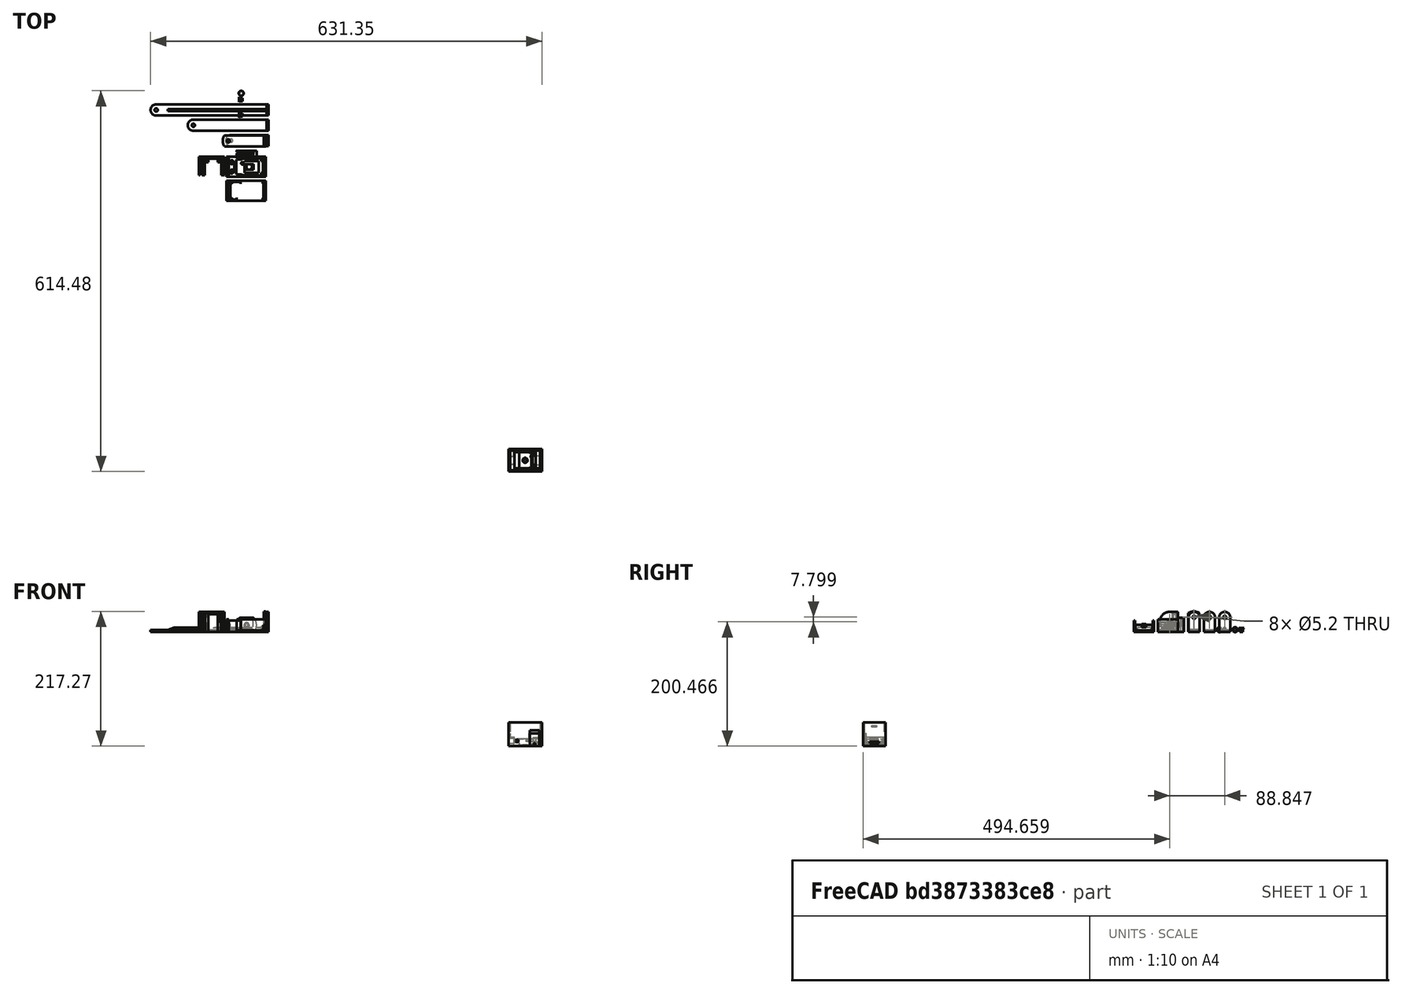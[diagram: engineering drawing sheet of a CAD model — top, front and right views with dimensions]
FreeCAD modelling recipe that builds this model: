
FCSTD DOCUMENT  (FreeCAD 0.18.4R)
Label: camera.wroover.nested
License: All rights reserved
LicenseURL: http://en.wikipedia.org/wiki/All_rights_reserved
objects: Part::Feature×27, Part::Extrusion×26, Part::FeaturePython×26, Part::Part2DObjectPython×23, Part::MultiFuse×20, Part::Cut×15, App::DocumentObjectGroup×10, Part::Cone×2
note: 139 computed .brp shape members not serialized (recipe doc carries the construction recipe); baked Part::Feature solids carry a one-line shape summary decoded from their .brp

FEATURE [Part::MultiFuse] Fusion005002002014004003003002009002010004002003006003008008004007002004008002005003003004011  label="Rail-Straight"
FEATURE [Part::Feature] Face
  Placement = pos=(-49.1911,484.37,17.9321) rot=(1,0,0;3.14159rad)
  shape: bbox 2.889e-06 x 7.275 x 8.4 mm, 1 faces, 0 solids (baked)
FEATURE [Part::Extrusion] Extrusion
  Base = -> Face
  Dir = (0.2,-6e-16,8e-16)
  DirMode = 0
  FaceMakerClass = Part::FaceMakerBullseye
  LengthFwd = 0
  LengthRev = 0
  Solid = true
  Symmetric = false
FEATURE [Part::MultiFuse] Fusion
  Shapes = -> [Extrusion,Fusion005002002014004003003002009002010004002003006003008008004007002004008002005003003004011]
FEATURE [Part::Feature] Face001
  Placement = pos=(-641.855,484.37,-5.97e-13) rot=(0,0,1;3.14159rad)
  shape: bbox 2.889e-06 x 7.275 x 8.4 mm, 1 faces, 0 solids (baked)
FEATURE [Part::Extrusion] Extrusion001
  Base = -> Face001
  Dir = (-0.2,-6e-16,-8e-16)
  DirMode = 0
  FaceMakerClass = Part::FaceMakerBullseye
  LengthFwd = 0
  LengthRev = 0
  Solid = true
  Symmetric = false
FEATURE [Part::MultiFuse] Fusion005002002014004003003002009002010004002003006003008008004007002004008002005003003004012
  Shapes = -> [Fusion,Extrusion001]
FEATURE [Part::Part2DObjectPython] Rectangle  # Draft 2D object (typed FeaturePython)
  ChamferSize = 0
  Columns = 1
  FilletRadius = 0
  Height = 80
  Length = 77
  MakeFace = true
  Placement = pos=(-363.417,362.38,-31.0339) rot=(0.57735,-0.57735,-0.57735;2.0944rad)
  Rows = 1
  Support = -> [Fusion005002002014004003003002009002010004002003006003008008004007002004008002005003003004012]
FEATURE [Part::FeaturePython] Slice  # WARN: FeaturePython — macro-defined, semantics opaque (R4)
  Base = -> Fusion005002002014004003003002009002010004002003006003008008004007002004008002005003003004012
  Mode = 1
  Tolerance = 0
  Tools = -> [Rectangle]
FEATURE [Part::FeaturePython] Slice_child0  label="Slice.0"  # WARN: FeaturePython — macro-defined, semantics opaque (R4)
  Base = -> Slice
  FilterType = 1
  Invert = false
  OverrideMaxVal = 0
  WindowFrom = 80
  WindowTo = 100
  items = 0
FEATURE [Part::FeaturePython] Slice_child1  label="Slice.1"  # WARN: FeaturePython — macro-defined, semantics opaque (R4)
  Base = -> Slice
  FilterType = 1
  Invert = false
  OverrideMaxVal = 0
  Placement = pos=(-3,0,-4e-15) rot=(0,0,1;0rad)
  WindowFrom = 80
  WindowTo = 100
  items = 1
FEATURE [Part::MultiFuse] Fusion005002002014004003003002009002010004002003006003008008004007002004008002005003003004009  label="Console"
  Placement = pos=(66.1287,37.5114,-1.47e-13) rot=(0,0,1;0rad)
FEATURE [Part::Part2DObjectPython] Rectangle001  # Draft 2D object (typed FeaturePython)
  ChamferSize = 0
  Columns = 1
  FilletRadius = 0
  Height = 49.0124
  Length = 71.1879
  MakeFace = true
  Placement = pos=(-260.782,380.747,-18.9904) rot=(0.57735,0.57735,0.57735;2.0944rad)
  Rows = 1
  Support = -> [Fusion005002002014004003003002009002010004002003006003008008004007002004008002005003003004009]
FEATURE [Part::Part2DObjectPython] Rectangle002  # Draft 2D object (typed FeaturePython)
  ChamferSize = 0
  Columns = 1
  FilletRadius = 0
  Height = 109.957
  Length = 144.352
  MakeFace = true
  Placement = pos=(-370.958,471.32,-6.63395) rot=(1,0,0;3.14159rad)
  Rows = 1
  Support = -> [Fusion005002002014004003003002009002010004002003006003008008004007002004008002005003003004009]
FEATURE [Part::FeaturePython] Slice001  # WARN: FeaturePython — macro-defined, semantics opaque (R4)
  Base = -> Fusion005002002014004003003002009002010004002003006003008008004007002004008002005003003004009
  Mode = 1
  Tolerance = 0
  Tools = -> [Rectangle002]
FEATURE [Part::FeaturePython] Slice001_child0  label="Slice001.0"  # WARN: FeaturePython — macro-defined, semantics opaque (R4)
  Base = -> Slice001
  FilterType = 1
  Invert = false
  OverrideMaxVal = 0
  WindowFrom = 80
  WindowTo = 100
  items = 0
FEATURE [App::DocumentObjectGroup] GrExplode_Slice001  label="Exploded Slice001"
  Group = -> [Slice001_child0]
FEATURE [Part::FeaturePython] Slice002  # WARN: FeaturePython — macro-defined, semantics opaque (R4)
  Base = -> Slice001_child0
  Mode = 1
  Tolerance = 0
  Tools = -> [Rectangle001]
FEATURE [Part::FeaturePython] Slice002_child0  label="Slice002.0"  # WARN: FeaturePython — macro-defined, semantics opaque (R4)
  Base = -> Slice002
  FilterType = 1
  Invert = false
  OverrideMaxVal = 0
  Placement = pos=(0,-35.1536,2.389e-13) rot=(0,0,1;0rad)
  WindowFrom = 80
  WindowTo = 100
  items = 0
FEATURE [App::DocumentObjectGroup] GrExplode_Slice002  label="Exploded Slice002"
  Group = -> [Slice002_child0]
FEATURE [Part::Part2DObjectPython] Rectangle003  # Draft 2D object (typed FeaturePython)
  ChamferSize = 0
  Columns = 1
  FilletRadius = 0
  Height = 32.2
  Length = 3.39945
  MakeFace = true
  Placement = pos=(-363.417,339.38,-7.13395) rot=(0.57735,-0.57735,-0.57735;2.0944rad)
  Rows = 1
  Support = -> [Slice_child0]
FEATURE [Part::Extrusion] Extrusion002
  Base = -> Rectangle003
  Dir = (-3,0,0)
  DirMode = 0
  FaceMakerClass = Part::FaceMakerBullseye
  LengthFwd = 0
  LengthRev = 0
  Solid = true
  Symmetric = false
FEATURE [Part::Part2DObjectPython] Wire  # Draft 2D object (typed FeaturePython)
  ChamferSize = 0
  Closed = true
  End = (-332.03,322.443,11.0661)
  FilletRadius = 0
  Length = 25.2
  MakeFace = true
  Placement = pos=(-332.03,322.443,6.86605) rot=(0.57735,-0.57735,-0.57735;2.0944rad)
  Points = (6) [(0,0,0),(-3.63731,-2.1,5.68434e-14),(-7.27461,3.4639e-14,5.68434e-14),(-7.27461,4.2,1.13687e-13),(-3.63731,6.3,1.13687e-13),(5.68434e-14,4.2,5.68434e-14)]
  Start = (-332.03,322.443,6.86605)
  Subdivisions = 0
  Support = -> [Slice_child0]
FEATURE [Part::Extrusion] Extrusion003
  Base = -> Wire
  Dir = (4.9,3.83e-14,4.42e-14)
  DirMode = 0
  FaceMakerClass = Part::FaceMakerBullseye
  LengthFwd = 0
  LengthRev = 0
  Solid = true
  Symmetric = false
FEATURE [Part::MultiFuse] Fusion005002002014004003003002009002010004002003006003008008004007002004008002005003003004013
  Shapes = -> [Slice_child0,Extrusion003]
FEATURE [Part::Feature] Fusion005002002014004003003002009002010004002003006003008008004007002004008002005003003004013001  label="Fusion005002002014004003003002009002010004002003006003008008004007002004008002005003003004014"
  shape: bbox 36.29 x 29.4 x 32.2 mm, 46 faces (baked)
FEATURE [Part::Feature] Face002
  shape: bbox 3.089e-06 x 29.4 x 32.2 mm, 1 faces, 0 solids (baked)
FEATURE [Part::Extrusion] Extrusion004
  Base = -> Face002
  Dir = (-1.9,-6.1e-15,-2.5e-15)
  DirMode = 0
  FaceMakerClass = Part::FaceMakerBullseye
  LengthFwd = 0
  LengthRev = 0
  Solid = true
  Symmetric = false
FEATURE [Part::Cut] Cut
  Base = -> Fusion005002002014004003003002009002010004002003006003008008004007002004008002005003003004013001
  Tool = -> Extrusion004
FEATURE [Part::Feature] Face003
  Placement = pos=(-48.7911,184.728,1.61e-13) rot=(0,0,1;0rad)
  shape: bbox 2.989e-06 x 29.4 x 32.2 mm, 1 faces, 0 solids (baked)
FEATURE [Part::Extrusion] Extrusion005
  Base = -> Face003
  Dir = (-1.5,4.8e-15,-2e-15)
  DirMode = 0
  FaceMakerClass = Part::FaceMakerBullseye
  LengthFwd = 0
  LengthRev = 0
  Solid = true
  Symmetric = false
FEATURE [Part::MultiFuse] Fusion005002002014004003003002009002010004002003006003008008004007002004008002005003003004013002
  Shapes = -> [Extrusion005,Slice_child1]
FEATURE [Part::MultiFuse] Fusion005002002014004003003002009002010004002003006003008008004007002004008002005003003004013003
  Shapes = -> [Fusion005002002014004003003002009002010004002003006003008008004007002004008002005003003004013002,Extrusion002,Cut]
FEATURE [App::DocumentObjectGroup] GrExplode_Slice  label="Exploded Slice"
  Group = -> [Fusion005002002014004003003002009002010004002003006003008008004007002004008002005003003004013,Fusion005002002014004003003002009002010004002003006003008008004007002004008002005003003004013003]
FEATURE [Part::Feature] Fusion005002002014004003003002009002010004002003006003008008004007002004008002005003003004013003001  label="Fusion005002002014004003003002009002010004002003006003008008004007002004008002005003003004013004"
  shape: bbox 39.39 x 29.4 x 32.2 mm, 51 faces (baked)
FEATURE [Part::Cone] Cone
  Angle = 360
  AttacherType = Attacher::AttachEngine3D
  Height = 2
  Placement = pos=(-301.953,406.671,-3.63395) rot=(0,-1,0;1.5708rad)
  Radius1 = 2.6
  Radius2 = 4
FEATURE [Part::Cone] Cone001
  Angle = 360
  AttacherType = Attacher::AttachEngine3D
  Height = 2
  Placement = pos=(-366.417,326.16,8.96605) rot=(0,-1,0;1.5708rad)
  Radius1 = 2.6
  Radius2 = 4
FEATURE [Part::Cut] Cut001
  Base = -> Fusion005002002014004003003002009002010004002003006003008008004007002004008002005003003004013003001
  Tool = -> Cone001
FEATURE [Part::Part2DObjectPython] Rectangle004  # Draft 2D object (typed FeaturePython)
  ChamferSize = 0
  Columns = 1
  FilletRadius = 0
  Height = 140.382
  Length = 142.339
  MakeFace = true
  Placement = pos=(-376.002,355.088,66.5569) rot=(-1,0,0;1.5708rad)
  Rows = 1
FEATURE [Part::Part2DObjectPython] Rectangle005  # Draft 2D object (typed FeaturePython)
  ChamferSize = 0
  Columns = 1
  FilletRadius = 0
  Height = 140.382
  Length = 142.339
  MakeFace = true
  Placement = pos=(-376.002,375.088,66.5569) rot=(-1,0,0;1.5708rad)
  Rows = 1
FEATURE [Part::FeaturePython] Slice003  # WARN: FeaturePython — macro-defined, semantics opaque (R4)
  Base = -> Slice002_child0
  Mode = 1
  Tolerance = 0
  Tools = -> [Rectangle005]
FEATURE [Part::FeaturePython] Slice003_child0  label="Slice003.0"  # WARN: FeaturePython — macro-defined, semantics opaque (R4)
  Base = -> Slice003
  FilterType = 1
  Invert = false
  OverrideMaxVal = 0
  WindowFrom = 80
  WindowTo = 100
  items = 0
FEATURE [App::DocumentObjectGroup] GrExplode_Slice003  label="Exploded Slice003"
  Group = -> [Slice003_child0]
FEATURE [Part::FeaturePython] Slice004  # WARN: FeaturePython — macro-defined, semantics opaque (R4)
  Base = -> Slice003_child0
  Mode = 1
  Tolerance = 0
  Tools = -> [Rectangle004]
FEATURE [Part::FeaturePython] Slice004_child0  label="Slice004.0"  # WARN: FeaturePython — macro-defined, semantics opaque (R4)
  Base = -> Slice004
  FilterType = 1
  Invert = false
  OverrideMaxVal = 0
  WindowFrom = 80
  WindowTo = 100
  items = 0
FEATURE [Part::Part2DObjectPython] Circle001  # Draft 2D object (typed FeaturePython)
  FirstAngle = 0
  LastAngle = 0
  MakeFace = true
  Placement = pos=(-263.782,365.088,9.58564) rot=(0.57735,-0.57735,-0.57735;2.0944rad)
  Radius = 4
FEATURE [Part::Extrusion] Extrusion006
  Base = -> Circle001
  Dir = (3,0,0)
  DirMode = 0
  FaceMakerClass = Part::FaceMakerBullseye
  LengthFwd = 0
  LengthRev = 0
  Solid = true
  Symmetric = false
FEATURE [Part::MultiFuse] Fusion005002002014004003003002009002010004002003006003008008004007002004008002005003003004013003002
  Shapes = -> [Slice004_child0,Extrusion006]
FEATURE [Part::Part2DObjectPython] Circle002  # Draft 2D object (typed FeaturePython)
  FirstAngle = 0
  LastAngle = 0
  MakeFace = true
  Placement = pos=(-301.953,406.671,-3.63395) rot=(0.57735,0.57735,0.57735;2.0944rad)
  Radius = 2.6
  Support = -> [Cone]
FEATURE [Part::Extrusion] Extrusion007
  Base = -> Circle002
  Dir = (4,0,0)
  DirMode = 0
  FaceMakerClass = Part::FaceMakerBullseye
  LengthFwd = 0
  LengthRev = 0
  Solid = true
  Symmetric = false
FEATURE [Part::MultiFuse] Fusion005002002014004003003002009002010004002003006003008008004007002004008002005003003004013003003
  Placement = pos=(0,25.1211,0) rot=(0,0,1;0rad)
  Shapes = -> [Cone,Extrusion007]
FEATURE [Part::MultiFuse] Fusion005002002014004003003002009002010004002003006003008008004007002004008002005003003004013003004
  Shapes = -> [Cone,Extrusion007]
FEATURE [Part::MultiFuse] Fusion005002002014004003003002009002010004002003006003008008004007002004008002005003003004013003005
  Placement = pos=(-64.6671,-80.5121,12.6) rot=(0,0,1;0rad)
  Shapes = -> [Cone,Extrusion007]
FEATURE [Part::Feature] Fusion005002002014004003003002009002010004002003006003008008004007002004008002005003003004013003004001  label="Fusion005002002014004003003002009002010004002003006003008008004007002004008002005003003004013003006"
  Placement = pos=(40.1704,-41.5836,20.3995) rot=(0,0,1;0rad)
  shape: bbox 6 x 8 x 8 mm, 4 faces (baked)
FEATURE [Part::Cut] Cut002
  Base = -> Fusion005002002014004003003002009002010004002003006003008008004007002004008002005003003004013003002
  Tool = -> Fusion005002002014004003003002009002010004002003006003008008004007002004008002005003003004013003004001
FEATURE [App::DocumentObjectGroup] GrExplode_Slice004  label="Exploded Slice004"
  Group = -> [Cut002]
FEATURE [Part::Part2DObjectPython] Rectangle006  # Draft 2D object (typed FeaturePython)
  ChamferSize = 0
  Columns = 1
  FilletRadius = 0
  Height = 141.963
  Length = 167.182
  MakeFace = true
  Placement = pos=(-347.373,356.088,87.747) rot=(-1,0,0;1.5708rad)
  Rows = 1
  Support = -> [Cut002]
FEATURE [Part::Part2DObjectPython] Rectangle007  # Draft 2D object (typed FeaturePython)
  ChamferSize = 0
  Columns = 1
  FilletRadius = 0
  Height = 141.963
  Length = 167.182
  MakeFace = true
  Placement = pos=(-347.373,374.088,87.747) rot=(-1,0,0;1.5708rad)
  Rows = 1
  Support = -> [Cut002]
FEATURE [Part::FeaturePython] Slice005  # WARN: FeaturePython — macro-defined, semantics opaque (R4)
  Base = -> Cut002
  Mode = 1
  Tolerance = 0
  Tools = -> [Rectangle007]
FEATURE [Part::FeaturePython] Slice005_child0  label="Slice005.0"  # WARN: FeaturePython — macro-defined, semantics opaque (R4)
  Base = -> Slice005
  FilterType = 1
  Invert = false
  OverrideMaxVal = 0
  WindowFrom = 80
  WindowTo = 100
  items = 0
FEATURE [App::DocumentObjectGroup] GrExplode_Slice005  label="Exploded Slice005"
  Group = -> [Slice005_child0]
FEATURE [Part::FeaturePython] Slice006  # WARN: FeaturePython — macro-defined, semantics opaque (R4)
  Base = -> Slice005_child0
  Mode = 1
  Tolerance = 0
  Tools = -> [Rectangle006]
FEATURE [Part::FeaturePython] Slice006_child0  label="Slice006.0"  # WARN: FeaturePython — macro-defined, semantics opaque (R4)
  Base = -> Slice006
  FilterType = 1
  Invert = false
  OverrideMaxVal = 0
  WindowFrom = 80
  WindowTo = 100
  items = 0
FEATURE [Part::Cut] Cut003  label="Frame"
  Tool = -> Extrusion
FEATURE [Part::Part2DObjectPython] Circle003  # Draft 2D object (typed FeaturePython)
  FirstAngle = 0
  LastAngle = 0
  MakeFace = true
  Placement = pos=(-263.782,365.088,16.7655) rot=(0.57735,-0.57735,-0.57735;2.0944rad)
  Radius = 4
FEATURE [Part::Extrusion] Extrusion008
  Base = -> Circle003
  Dir = (2,0,0)
  DirMode = 0
  FaceMakerClass = Part::FaceMakerBullseye
  LengthFwd = 0
  LengthRev = 0
  Solid = true
  Symmetric = false
FEATURE [Part::MultiFuse] Fusion005002002014004003003002009002010004002003006003008008004007002004008002005003003004013003004002
  Shapes = -> [Extrusion008,Slice006_child0]
FEATURE [Part::Part2DObjectPython] Circle004  # Draft 2D object (typed FeaturePython)
  FirstAngle = 0
  LastAngle = 0
  MakeFace = true
  Placement = pos=(-260.782,365.088,16.7655) rot=(0.57735,0.57735,0.57735;2.0944rad)
  Radius = 2.6
FEATURE [Part::Extrusion] Extrusion009
  Base = -> Circle004
  Dir = (-9.48538,0,0)
  DirMode = 0
  FaceMakerClass = Part::FaceMakerBullseye
  LengthFwd = 0
  LengthRev = 0
  Solid = true
  Symmetric = false
FEATURE [Part::Cut] Cut004
  Base = -> Fusion005002002014004003003002009002010004002003006003008008004007002004008002005003003004013003004002
  Tool = -> Extrusion009
FEATURE [Part::Feature] Face004
  shape: bbox 32.2 x 4.069e-06 x 22.84 mm, 1 faces, 0 solids (baked)
FEATURE [Part::Feature] Face005
  Placement = pos=(-2.1881e-12,3,2.9e-14) rot=(0,0,1;0rad)
  shape: bbox 32.2 x 4.069e-06 x 22.84 mm, 1 faces, 0 solids (baked)
FEATURE [Part::Extrusion] Extrusion011
  Base = -> Face005
  Dir = (-1.4587e-12,2,1.94e-14)
  DirMode = 0
  FaceMakerClass = Part::FaceMakerBullseye
  LengthFwd = 0
  LengthRev = 0
  Solid = true
  Symmetric = false
FEATURE [Part::Part2DObjectPython] Rectangle008  # Draft 2D object (typed FeaturePython)
  ChamferSize = 0
  Columns = 1
  FilletRadius = 0
  Height = 132.663
  Length = 70.7455
  MakeFace = true
  Placement = pos=(-281.653,308.795,-48.4256) rot=(0.57735,0.57735,0.57735;2.0944rad)
  Rows = 1
  Support = -> [Cut003]
FEATURE [Part::FeaturePython] Slice007  # WARN: FeaturePython — macro-defined, semantics opaque (R4)
  Base = -> Extrusion011
  Mode = 1
  Tolerance = 0
  Tools = -> [Rectangle008]
FEATURE [Part::FeaturePython] Slice007_child0  label="Slice007.0"  # WARN: FeaturePython — macro-defined, semantics opaque (R4)
  Base = -> Slice007
  FilterType = 1
  Invert = false
  OverrideMaxVal = 0
  WindowFrom = 80
  WindowTo = 100
  items = 0
FEATURE [Part::FeaturePython] Slice007_child1  label="Slice007.1"  # WARN: FeaturePython — macro-defined, semantics opaque (R4)
  Base = -> Slice007
  FilterType = 1
  Invert = false
  OverrideMaxVal = 0
  WindowFrom = 80
  WindowTo = 100
  items = 1
FEATURE [Part::Feature] Face006
  shape: bbox 6.28 x 4.169e-06 x 22.84 mm, 1 faces, 0 solids (baked)
FEATURE [Part::Extrusion] Extrusion012
  Base = -> Face006
  Dir = (2.1881e-12,-3,-2.9e-14)
  DirMode = 0
  FaceMakerClass = Part::FaceMakerBullseye
  LengthFwd = 0
  LengthRev = 0
  Solid = true
  Symmetric = false
FEATURE [Part::Feature] Face007
  shape: bbox 6.28 x 4.169e-06 x 22.84 mm, 1 faces, 0 solids (baked)
FEATURE [Part::Extrusion] Extrusion013
  Base = -> Face007
  Dir = (-1.459e-13,0.2,1.9e-15)
  DirMode = 0
  FaceMakerClass = Part::FaceMakerBullseye
  LengthFwd = 0
  LengthRev = 0
  Solid = true
  Symmetric = false
FEATURE [Part::Feature] Face008
  shape: bbox 25.92 x 4.169e-06 x 22.84 mm, 1 faces, 0 solids (baked)
FEATURE [Part::Extrusion] Extrusion014
  Base = -> Face008
  Dir = (-1.459e-13,0.2,1.9e-15)
  DirMode = 0
  FaceMakerClass = Part::FaceMakerBullseye
  LengthFwd = 0
  LengthRev = 0
  Solid = true
  Symmetric = false
FEATURE [Part::MultiFuse] Fusion005002002014004003003002009002010004002003006003008008004007002004008002005003003004013003004003
  Shapes = -> [Extrusion014,Extrusion013,Slice007_child1,Slice007_child0,Extrusion012,Cut003]
FEATURE [Part::Feature] Face009
  shape: bbox 3.089e-06 x 29.4 x 32.2 mm, 1 faces, 0 solids (baked)
FEATURE [Part::Extrusion] Extrusion015
  Base = -> Face009
  Dir = (-0.202869,7e-16,-3e-16)
  DirMode = 0
  FaceMakerClass = Part::FaceMakerBullseye
  LengthFwd = 0
  LengthRev = 0
  Solid = true
  Symmetric = false
FEATURE [Part::Part2DObjectPython] Circle005  # Draft 2D object (typed FeaturePython)
  FirstAngle = 0
  LastAngle = 0
  MakeFace = true
  Placement = pos=(-368.62,326.159,8.96605) rot=(0.57735,-0.57735,-0.57735;2.0944rad)
  Radius = 4
FEATURE [Part::Extrusion] Extrusion016
  Base = -> Circle005
  Dir = (2.20287,0,0)
  DirMode = 0
  FaceMakerClass = Part::FaceMakerBullseye
  LengthFwd = 0
  LengthRev = 0
  Solid = true
  Symmetric = false
FEATURE [Part::MultiFuse] Fusion005002002014004003003002009002010004002003006003008008004007002004008002005003003004013003004004
  Shapes = -> [Extrusion015,Extrusion016]
FEATURE [Part::MultiFuse] Fusion005002002014004003003002009002010004002003006003008008004007002004008002005003003004013003004005
  Shapes = -> [Fusion005002002014004003003002009002010004002003006003008008004007002004008002005003003004013003004004,Cut001]
FEATURE [Part::Cut] Cut005
  Base = -> Fusion005002002014004003003002009002010004002003006003008008004007002004008002005003003004013003004005
  Tool = -> Fusion005002002014004003003002009002010004002003006003008008004007002004008002005003003004013003005
FEATURE [Part::Feature] Fusion005002002014004003003002009002010004002003006003008008004007002004008002005003003004013003003001  label="Fusion005002002014004003003002009002010004002003006003008008004007002004008002005003003004013003004006"
  Placement = pos=(-723.266,45.4151,7.39306) rot=(0,0,-1;1.5708rad)
  shape: bbox 8 x 6 x 8 mm, 4 faces (baked)
FEATURE [Part::Feature] Fusion005002002014004003003002009002010004002003006003008008004007002004008002005003003004013003004006  label="Fusion005002002014004003003002009002010004002003006003008008004007002004008002005003003004013003004007"
  shape: bbox 6 x 8 x 8 mm, 4 faces (baked)
FEATURE [Part::Feature] Fusion005002002014004003003002009002010004002003006003008008004007002004008002005003003004013003004007  label="Fusion005002002014004003003002009002010004002003006003008008004007002004008002005003003004013003004008"
  Placement = pos=(-296.517,10.1875,-305.087) rot=(0,1,0;1.5708rad)
  shape: bbox 8 x 8 x 6 mm, 4 faces (baked)
FEATURE [Part::Cut] Cut006
  Base = -> Fusion005002002014004003003002009002010004002003006003008008004007002004008002005003003004013003004003
  Tool = -> Fusion005002002014004003003002009002010004002003006003008008004007002004008002005003003004013003003001
FEATURE [App::DocumentObjectGroup] GrExplode_Slice007  label="Exploded Slice007"
  Group = -> [Cut006]
FEATURE [Part::Part2DObjectPython] Circle006  # Draft 2D object (typed FeaturePython)
  FirstAngle = 0
  LastAngle = 0
  MakeFace = true
  Placement = pos=(-313.782,365.088,-3.63395) rot=(0,0,1;0rad)
  Radius = 4
  Support = -> [Cut004]
FEATURE [Part::Extrusion] Extrusion017
  Base = -> Circle006
  Dir = (4.9e-15,-2.04e-14,-3)
  DirMode = 0
  FaceMakerClass = Part::FaceMakerBullseye
  LengthFwd = 0
  LengthRev = 0
  Solid = true
  Symmetric = false
FEATURE [Part::MultiFuse] Fusion005002002014004003003002009002010004002003006003008008004007002004008002005003003004013003004008  label="Fusion005002002014004003003002009002010004002003006003008008004007002004008002005003003004013003004009"
  Shapes = -> [Cut004,Extrusion017]
FEATURE [Part::Part2DObjectPython] Circle007  # Draft 2D object (typed FeaturePython)
  FirstAngle = 0
  LastAngle = 0
  MakeFace = true
  Placement = pos=(-320.882,365.088,-3.63395) rot=(0,0,1;0rad)
  Radius = 2.6
  Support = -> [Fusion005002002014004003003002009002010004002003006003008008004007002004008002005003003004013003004008]
FEATURE [Part::Extrusion] Extrusion018
  Base = -> Circle007
  Dir = (3.6e-14,-1.514e-13,-22.2274)
  DirMode = 0
  FaceMakerClass = Part::FaceMakerBullseye
  LengthFwd = 0
  LengthRev = 0
  Solid = true
  Symmetric = false
FEATURE [Part::Cut] Cut007
  Base = -> Fusion005002002014004003003002009002010004002003006003008008004007002004008002005003003004013003004008
  Tool = -> Extrusion018
FEATURE [App::DocumentObjectGroup] GrExplode_Slice006  label="Exploded Slice006"
  Group = -> [Cut007]
FEATURE [Part::Feature] Cut007001  label="Cut008"
  shape: bbox 69.1 x 18 x 32.4 mm, 11 faces (baked)
FEATURE [Part::Feature] Face010
  shape: bbox 69.1 x 18 x 2.989e-06 mm, 1 faces, 0 solids (baked)
FEATURE [Part::Extrusion] Extrusion019
  Base = -> Face010
  Dir = (-2e-16,7e-16,0.1)
  DirMode = 0
  FaceMakerClass = Part::FaceMakerBullseye
  LengthFwd = 0
  LengthRev = 0
  Solid = true
  Symmetric = false
FEATURE [Part::Cut] Cut007002
  Base = -> Cut007001
  Tool = -> Extrusion019
FEATURE [Part::Feature] Face011
  shape: bbox 2.989e-06 x 18 x 32.3 mm, 1 faces, 0 solids (baked)
FEATURE [Part::Extrusion] Extrusion020
  Base = -> Face011
  Dir = (-0.1,0,0)
  DirMode = 0
  FaceMakerClass = Part::FaceMakerBullseye
  LengthFwd = 0
  LengthRev = 0
  Solid = true
  Symmetric = false
FEATURE [Part::Cut] Cut007003
  Base = -> Cut007002
  Tool = -> Extrusion020
FEATURE [Part::Part2DObjectPython] Circle008  # Draft 2D object (typed FeaturePython)
  FirstAngle = 0
  LastAngle = 0
  MakeFace = true
  Placement = pos=(-320.882,365.088,-3.63395) rot=(0,0,1;0rad)
  Radius = 9
  Support = -> [Cut007003]
FEATURE [Part::Part2DObjectPython] Circle009  # Draft 2D object (typed FeaturePython)
  FirstAngle = 0
  LastAngle = 0
  MakeFace = true
  Placement = pos=(-320.882,365.088,-3.63395) rot=(0,0,1;0rad)
  Radius = 15.8248
FEATURE [Part::Extrusion] Extrusion021
  Base = -> Circle009
  Dir = (4.7e-14,-8.63e-14,-15.1489)
  DirMode = 0
  FaceMakerClass = Part::FaceMakerBullseye
  LengthFwd = 0
  LengthRev = 0
  Solid = true
  Symmetric = false
FEATURE [Part::Extrusion] Extrusion022
  Base = -> Circle008
  Dir = (4.7e-14,-8.63e-14,-15.1489)
  DirMode = 0
  FaceMakerClass = Part::FaceMakerBullseye
  LengthFwd = 0
  LengthRev = 0
  Solid = true
  Symmetric = false
FEATURE [Part::Cut] Cut007004
  Base = -> Extrusion021
  Tool = -> Extrusion022
FEATURE [Part::Part2DObjectPython] Rectangle009  # Draft 2D object (typed FeaturePython)
  ChamferSize = 0
  Columns = 1
  FilletRadius = 0
  Height = 131.25
  Length = 208.758
  MakeFace = true
  Placement = pos=(-320.882,469.467,-69.259) rot=(0.57735,-0.57735,-0.57735;2.0944rad)
  Rows = 1
  Support = -> [Cut007003]
FEATURE [Part::FeaturePython] Slice008  # WARN: FeaturePython — macro-defined, semantics opaque (R4)
  Base = -> Cut007004
  Mode = 1
  Tolerance = 0
  Tools = -> [Rectangle009]
FEATURE [Part::FeaturePython] Slice008_child0  label="Slice008.0"  # WARN: FeaturePython — macro-defined, semantics opaque (R4)
  Base = -> Slice008
  FilterType = 1
  Invert = false
  OverrideMaxVal = 0
  Placement = pos=(-267.416,1.296e-11,337.648) rot=(0,-1,0;1.5708rad)
  WindowFrom = 80
  WindowTo = 100
  items = 0
FEATURE [Part::FeaturePython] Slice008_child1  label="Slice008.1"  # WARN: FeaturePython — macro-defined, semantics opaque (R4)
  Base = -> Slice008
  FilterType = 1
  Invert = false
  OverrideMaxVal = 0
  WindowFrom = 80
  WindowTo = 100
  items = 1
FEATURE [Part::Cut] Cut007005
  Base = -> Cut007003
  Tool = -> Slice008_child0
FEATURE [Part::Cut] Cut007006
  Base = -> Cut007005
  Placement = pos=(4.52481,0.516273,-0.6) rot=(0,0,1;0rad)
  Tool = -> Slice008_child1
FEATURE [App::DocumentObjectGroup] GrExplode_Slice008  label="Exploded Slice008"
  Group = -> [Cut007006]
FEATURE [Part::Feature] Cut005001  label="Cut007007"
  shape: bbox 39.59 x 29.4 x 32.2 mm, 57 faces (baked)
FEATURE [Part::Feature] Cut006001  label="Cut007008"
  shape: bbox 63.8 x 42.3 x 22.84 mm, 123 faces (baked)
FEATURE [Part::Feature] Cut007006001  label="Cut007009"
  Placement = pos=(0,24.8307,4.62e-14) rot=(0,0,1;0rad)
  shape: bbox 69 x 18 x 32.3 mm, 11 faces (baked)
FEATURE [Part::Feature] Cut007006002  label="Cut007010"
  shape: bbox 69 x 18 x 32.3 mm, 11 faces (baked)
FEATURE [Part::Part2DObjectPython] Rectangle010  # Draft 2D object (typed FeaturePython)
  ChamferSize = 0
  Columns = 1
  FilletRadius = 0
  Height = 125.613
  Length = 111.778
  MakeFace = true
  Placement = pos=(-264.257,455.324,-67.0405) rot=(0.57735,-0.57735,-0.57735;2.0944rad)
  Rows = 1
  Support = -> [Cut007006001]
FEATURE [Part::FeaturePython] Slice009  # WARN: FeaturePython — macro-defined, semantics opaque (R4)
  Base = -> Cut007006001
  Mode = 1
  Tolerance = 0
  Tools = -> [Rectangle010]
FEATURE [Part::FeaturePython] Slice009_child0  label="Slice009.0"  # WARN: FeaturePython — macro-defined, semantics opaque (R4)
  Base = -> Slice009
  FilterType = 1
  Invert = false
  OverrideMaxVal = 0
  Placement = pos=(-121,24.5719,-3.642e-13) rot=(0,0,1;0rad)
  WindowFrom = 80
  WindowTo = 100
  items = 0
FEATURE [Part::FeaturePython] Slice009_child1  label="Slice009.1"  # WARN: FeaturePython — macro-defined, semantics opaque (R4)
  Base = -> Slice009
  FilterType = 1
  Invert = false
  OverrideMaxVal = 0
  Placement = pos=(0,24.5719,-1.67e-13) rot=(0,0,1;0rad)
  WindowFrom = 80
  WindowTo = 100
  items = 1
FEATURE [Part::Feature] Face012
  shape: bbox 4e-07 x 18 x 2.9 mm, 1 faces, 0 solids (baked)
FEATURE [Part::Extrusion] Extrusion023
  Base = -> Face012
  Dir = (-61,0,0)
  DirMode = 0
  FaceMakerClass = Part::FaceMakerBullseye
  LengthFwd = 0
  LengthRev = 0
  Solid = true
  Symmetric = false
FEATURE [Part::FeaturePython] Slice009_child002  label="Slice009.002"  # WARN: FeaturePython — macro-defined, semantics opaque (R4)
  Base = -> Slice009
  FilterType = 1
  Invert = false
  OverrideMaxVal = 0
  WindowFrom = 80
  WindowTo = 100
  items = 1
FEATURE [Part::FeaturePython] Slice009_child003  label="Slice009.003"  # WARN: FeaturePython — macro-defined, semantics opaque (R4)
  Base = -> Slice009
  FilterType = 1
  Invert = false
  OverrideMaxVal = 0
  Placement = pos=(-61,0,-9.9e-14) rot=(0,0,1;0rad)
  WindowFrom = 80
  WindowTo = 100
  items = 0
FEATURE [Part::Feature] Face013
  Placement = pos=(0,24.5719,-1.67e-13) rot=(0,0,1;0rad)
  shape: bbox 4e-07 x 18 x 2.9 mm, 1 faces, 0 solids (baked)
FEATURE [Part::Extrusion] Extrusion024
  Base = -> Face013
  Dir = (-121,0,0)
  DirMode = 0
  FaceMakerClass = Part::FaceMakerBullseye
  LengthFwd = 0
  LengthRev = 0
  Solid = true
  Symmetric = false
FEATURE [Part::MultiFuse] Fusion005002002014004003003002009002010004002003006003008008004007002004008002005003003004013003004009  label="Fusion005002002014004003003002009002010004002003006003008008004007002004008002005003003004013003004010"
  Shapes = -> [Slice009_child1,Extrusion024,Slice009_child0]
FEATURE [Part::MultiFuse] Fusion005002002014004003003002009002010004002003006003008008004007002004008002005003003004013003004010  label="Fusion005002002014004003003002009002010004002003006003008008004007002004008002005003003004013003004011"
  Shapes = -> [Slice009_child002,Extrusion023,Slice009_child003]
FEATURE [Part::Part2DObjectPython] Rectangle012  # Draft 2D object (typed FeaturePython)
  ChamferSize = 0
  Columns = 1
  FilletRadius = 0
  Height = 160
  Length = 3
  MakeFace = true
  Placement = pos=(-258.357,413.507,-4.23395) rot=(0,0,1;1.5708rad)
  Rows = 1
  Support = -> [Fusion005002002014004003003002009002010004002003006003008008004007002004008002005003003004013003004009]
FEATURE [Part::Extrusion] Extrusion025
  Base = -> Rectangle012
  Dir = (-1.6e-15,1.58e-14,4)
  DirMode = 0
  FaceMakerClass = Part::FaceMakerBullseye
  LengthFwd = 0
  LengthRev = 0
  Solid = true
  Symmetric = false
FEATURE [Part::MultiFuse] Fusion005002002014004003003002009002010004002003006003008008004007002004008002005003003004013003004011  label="Fusion005002002014004003003002009002010004002003006003008008004007002004008002005003003004013003004012"
  Shapes = -> [Extrusion025,Fusion005002002014004003003002009002010004002003006003008008004007002004008002005003003004013003004009]
FEATURE [Part::Part2DObjectPython] Wire001  # Draft 2D object (typed FeaturePython)
  ChamferSize = 0
  Closed = true
  End = (-418.357,416.507,-0.233948)
  FilletRadius = 0
  Length = 24.7703
  MakeFace = true
  Placement = pos=(-408.357,416.507,-0.233948) rot=(-1,0,0;1.5708rad)
  Points = (3) [(0,0,0),(-10,4,5.68434e-14),(-10,4.41314e-15,0)]
  Start = (-408.357,416.507,-0.233948)
  Subdivisions = 0
FEATURE [Part::Extrusion] Extrusion026
  Base = -> Wire001
  Dir = (-9e-16,-28.381,-2.017e-13)
  DirMode = 0
  FaceMakerClass = Part::FaceMakerBullseye
  LengthFwd = 0
  LengthRev = 0
  Solid = true
  Symmetric = false
FEATURE [Part::Cut] Cut007006003
  Base = -> Fusion005002002014004003003002009002010004002003006003008008004007002004008002005003003004013003004011
  Tool = -> Extrusion026
FEATURE [App::DocumentObjectGroup] GrExplode_Slice009  label="Exploded Slice009"
  Group = -> [Cut007006003]
FEATURE [Part::Feature] Cut007006003001  label="Cut007006004"
  shape: bbox 190 x 18 x 32.3 mm, 15 faces (baked)
FEATURE [Part::Feature] Fusion005002002014004003003002009002010004002003006003008008004007002004008002005003003004013003004010001  label="Fusion005002002014004003003002009002010004002003006003008008004007002004008002005003003004013003004013"
  shape: bbox 130 x 18 x 32.3 mm, 11 faces (baked)
FEATURE [Part::Cut] Cut004008021006004001003007003
  Tool = -> Extrusion022
FEATURE [Part::MultiFuse] Fusion005002002014004003003002009002010004002003006003008008004007002004008002005003003004019003004
  Placement = pos=(0,-78.0553,-2.54e-13) rot=(0,0,1;0rad)
  Shapes = -> [Extrusion007]
